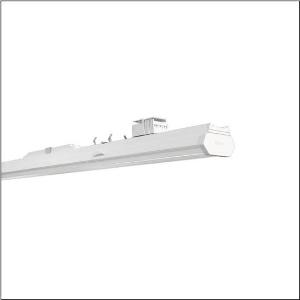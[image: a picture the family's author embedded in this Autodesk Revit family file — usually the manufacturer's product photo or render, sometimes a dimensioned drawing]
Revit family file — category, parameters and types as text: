
# Revit family: licross_r__11_protected_ho_51tp12dn5exl_83db
name_source: partatom
category: Lighting Fixtures
units: mm (PartAtom-declared; Revit-internal decimal feet)

## family parameters
Cut with Voids When Loaded = No
Host = Face
Light Source = No
Part Type = Normal
Room Calculation Point = No
Round Connector Dimension = Use Diameter
Shared = No

## types (1)
- --- (1 x LED, 14100 lm, 86.1 W, 5000K)
    Apparent Load = 86 VA
    CIE Flux Codes = 70 91 97 98 100
    Color Rendering = 80
    Color Temperature = 5000K
    Default Elevation = 1800 mm
    Description = Licross® 11 Protected HO, luminaire insert, of sheet steel, galvanised, coil coated, white, length: 1.500mm, width: 90mm, height: 101mm, LED rated luminous flux: 14.100lm, light colour: 850, control gear: DALI 2, control gear: ECG DALI, with plug, 5-pole, with phase selection, mains connection: 220..240V, AC, 50/60Hz, rated input power: 86W, halogen-free wiring, primary optical cover: cover, of PMMA, light emission: direct distribution, primary light characteristic: symmetric, protection rating (complete): IP64, insulation class (complete): insulation class I (protective earthing), certification: CE, ENEC, VDE, UKCA, protection symbol: D if used in an environment with conductive dust loads with corresponding accessories, impact resistance: IK06, permissible ambient temperature for indoor applications: -25..+35°C, reducing of maximum allowable ambient temperature of 5°C with ceiling mounting, corresponds to IFS (International Featured Standards) requirements for safety and quality in the food industry, LABS conformity tested according to VDMA 24364:2018-05, packaging unit: 1 piece
    Height = 92 mm
    Lamp = 1 x LED
    Lamp Light Flux = 14100 lm
    Lamp Power = 86.1 W
    Lamp count = 1
    Length = 1500 mm
    Luminous efficacy = 164 lm/W
    Manufacturer = Siteco
    ModVariant = No
    Model = 51TP12DN5EXL
    Mounting Place = Ceiling
    Mounting Type = Pendant
    Number of Poles = 1
    OnlyDefault = Yes
    Power Factor = 1
    Product Name = Licross® 11 Protected HO
    Product group = luminaire insert
    ProductGroupID = 901
    Protection Class = Protection class I
    Protection Degree = IP 64
    RLX_Detail_Level = 1
    RLX_Emergency_Light_Flux = 0 lm
    RLX_Emergency_Type = 0
    RLX_Emergency_Type_DB = No
    RlxData = <blob elided: 24277 chars, md5=2c40d6a8>
    Socket = socket
    Standby Power = 0 W
    System Light Flux = 14100 lm
    System Power = 86 W
    Type Comments = factory setting: luminous flux: 100 % | dim-lin: 254 | 485 mA
    Type Image = l_1256148.jpg
    URL = http://relux.com
    VarID = @adj_143657
    Voltage = 0 V
    Weight = 0.00 kg
    Width = 88 mm

## geometry (parser evidence)
native form markers: Blend x4, Sweep x10
no freeform markers — native parametric forms only
